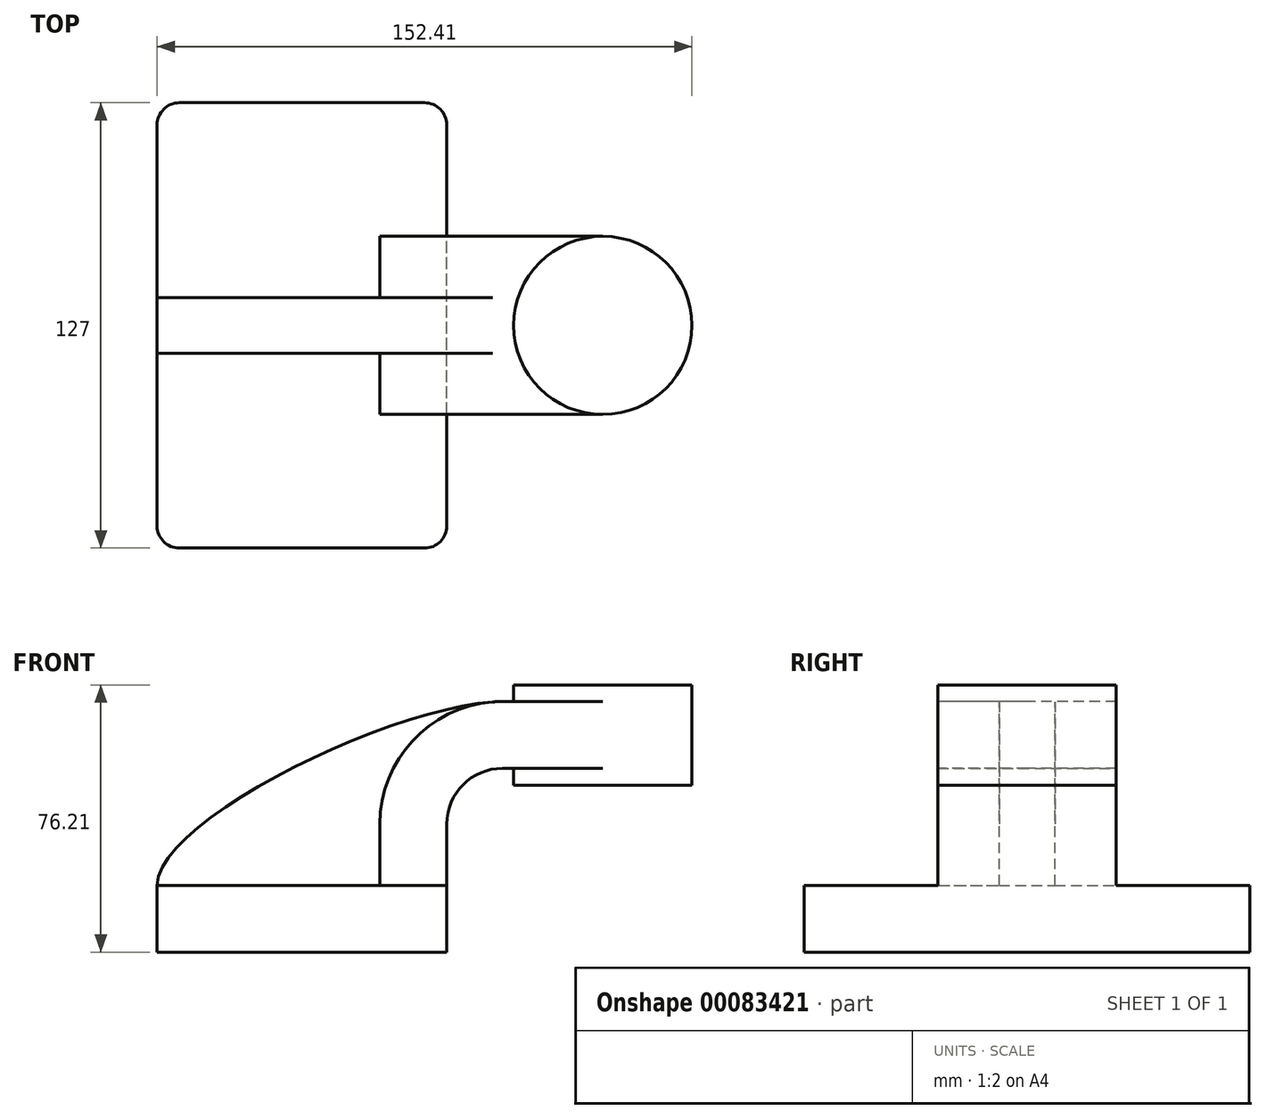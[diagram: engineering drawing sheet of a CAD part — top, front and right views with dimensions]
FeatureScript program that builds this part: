
annotation { "Feature Type Name" : "Feature", "Feature Type Description" : "" }
export const myFeature = defineFeature(function(context is Context, id is Id, definition is map)
    precondition{}
    {
        {
            var Q0;
            Q0=qCreatedBy(makeId("Front.planeOp"),FACE);
            var sketch = newSketch(context, id + "F0", { "sketchPlane" : qUnion([Q0])});
            skLineSegment(sketch, "E0.bottom", {"start": v(-41.28, -9.53) * mm, "end": v(41.28, -9.53) * mm});
            skLineSegment(sketch, "E0.top", {"start": v(-41.28, 9.53) * mm, "end": v(41.27, 9.53) * mm});
            skLineSegment(sketch, "E0.left", {"start": v(-41.27, -9.53) * mm, "end": v(-41.28, 9.53) * mm});
            skLineSegment(sketch, "E0.right", {"start": v(41.28, -9.53) * mm, "end": v(41.27, 9.53) * mm});
            skPoint(sketch, "E0.middle", {"position": v(0, 0) * mm});
            skLineSegment(sketch, "E1.bottom", {"start": v(60.33, 38.1) * mm, "end": v(111.13, 38.1) * mm});
            skLineSegment(sketch, "E1.top", {"start": v(60.32, 66.67) * mm, "end": v(111.13, 66.67) * mm});
            skLineSegment(sketch, "E1.left", {"start": v(60.33, 38.1) * mm, "end": v(60.33, 66.68) * mm});
            skLineSegment(sketch, "E1.right", {"start": v(111.13, 38.1) * mm, "end": v(111.13, 66.68) * mm});
            skPoint(sketch, "E1.middle", {"position": v(85.73, 52.39) * mm});
            skLineSegment(sketch, "E2", {"start": v(41.27, 9.53) * mm, "end": v(41.27, 27) * mm});
            skArc(sketch, "E3", {"start": v(41.27, 27) * mm, "mid": v(45.92, 38.23) * mm, "end": v(57.15, 42.88) * mm});
            skLineSegment(sketch, "E4", {"start": v(57.15, 42.88) * mm, "end": v(85.72, 42.88) * mm});
            skLineSegment(sketch, "E5.0", {"start": v(57.15, 61.93) * mm, "end": v(85.72, 61.93) * mm});
            skArc(sketch, "E5.1", {"start": v(22.23, 27) * mm, "mid": v(32.45, 51.7) * mm, "end": v(57.15, 61.93) * mm});
            skLineSegment(sketch, "E5.2", {"start": v(22.23, 9.53) * mm, "end": v(22.23, 27) * mm});
            skLineSegment(sketch, "E6", {"start": v(85.73, 38.1) * mm, "end": v(85.73, 66.67) * mm});
            skFitSpline(sketch, "E7", {"points": [v(-41.28, 9.52) * mm, v(57.15, 61.93) * mm], "startDerivative": vector(0.81, 57.71) * mm, "endDerivative": vector(87.68, 0.7) * mm});
            skSolve(sketch);
        }
        {
            var Q0;
            Q0=makeQuery(id+"F0.imprint","IMPRINT",FACE,{"disambiguationData":[TD([[makeQuery(id+"F0.imprint","IMPRINT",EDGE,{"derivedFrom":sQuery(id+"F0.wireOp",EDGE,"E0.bottom")}),1.0]])]});
            extrude(context, id + "F1", {"entities" : qUnion([Q0]), "endBound" : BoundingType.SYMMETRIC, "depth" : 127 * mm});
        }
        {
            var Q0;
            {var subQ1=sQuery(id+"F0.wireOp",EDGE,"E2");Q0=makeQuery(id+"F0.imprint","IMPRINT",FACE,{"disambiguationData":[TD([[makeQuery(id+"F0.imprint","IMPRINT",EDGE,{"derivedFrom":subQ1}),1.0]])]});}
            var Q1;
            {var subQ0=sQuery(id+"F0.wireOp",EDGE,"E4");var subQ1=sQuery(id+"F0.wireOp",EDGE,"E1.left");var subQ2=makeQuery(id+"F0.imprint","INTERSECT",VERTEX,{"derivedFrom":[subQ1,subQ0]});Q1=makeQuery(id+"F0.imprint","IMPRINT",FACE,{"disambiguationData":[TD([[makeQuery(id+"F0.imprint","IMPRINT",EDGE,{"disambiguationData":[TD([[subQ2,-1.0]])],"derivedFrom":subQ1}),-1.0]])]});}
            extrude(context, id + "F2", {"entities" : qUnion([Q0, Q1]), "operationType" : NewBodyOperationType.ADD, "endBound" : BoundingType.SYMMETRIC, "depth" : 50.8 * mm});
        }
        {
            var Q0;
            {var subQ3=sQuery(id+"F0.wireOp",EDGE,"E5.2");Q0=makeQuery(id+"F0.imprint","IMPRINT",FACE,{"disambiguationData":[TD([[makeQuery(id+"F0.imprint","IMPRINT",EDGE,{"derivedFrom":subQ3}),1.0]])]});}
            extrude(context, id + "F3", {"entities" : qUnion([Q0]), "operationType" : NewBodyOperationType.ADD, "endBound" : BoundingType.SYMMETRIC, "depth" : 15.88 * mm});
        }
        {
            var Q0;
            {var subQ0=sQuery(id+"F0.wireOp",EDGE,"E1.right");Q0=makeQuery(id+"F0.imprint","IMPRINT",FACE,{"disambiguationData":[TD([[makeQuery(id+"F0.imprint","IMPRINT",EDGE,{"derivedFrom":subQ0}),1.0]])]});}
            var Q1;
            Q1=sQuery(id+"F0.wireOp",EDGE,"E6");
            revolve(context, id + "F4", {"operationType" : NewBodyOperationType.ADD, "entities" : qUnion([Q0]), "axis" : qUnion([Q1]), "revolveType" : RevolveType.FULL});
        }
        {
            var Q0;
            Q0=makeQuery(id+"F1.opExtrude","CAP_EDGE",EDGE,{"disambiguationData":[OSD([sQuery(id+"F0.wireOp",EDGE,"E0.left")])],"isStart":false});
            var Q1;
            Q1=makeQuery(id+"F1.opExtrude","CAP_EDGE",EDGE,{"disambiguationData":[OSD([sQuery(id+"F0.wireOp",EDGE,"E0.right")])],"isStart":false});
            var Q2;
            Q2=makeQuery(id+"F1.opExtrude","CAP_EDGE",EDGE,{"disambiguationData":[OSD([sQuery(id+"F0.wireOp",EDGE,"E0.right")])],"isStart":true});
            var Q3;
            Q3=makeQuery(id+"F1.opExtrude","CAP_EDGE",EDGE,{"disambiguationData":[OSD([sQuery(id+"F0.wireOp",EDGE,"E0.left")])],"isStart":true});
            fillet(context, id + "F5", {"entities" : qUnion([Q0, Q1, Q2, Q3]), "radius" : 6.35 * mm, "tangentPropagation" : true, "allowEdgeOverflow" : false});
        }
    });
